# Revit family: Haworth_XSeries_Pedestal
name_source: partatom
category: Furniture Systems
units: mm (PartAtom-declared; Revit-internal decimal feet)

## family parameters
Always vertical = Yes
Cut with Voids When Loaded = No
OmniClass Number = 23.40.70.14.64.21
OmniClass Title = Systems Furniture
Part Type = Normal
Room Calculation Point = No
Round Connector Dimension = Use Diameter
Shared = No
Work Plane-Based = No

## types (10) — shared parameters
2 Drawers = Yes
Actual Depth = 23"
Actual Width = 15"
Assembly Code = E2020200
Classic Pull = No
Crescent Pull = No
Custom Size = No
Depth = 23"
Description = Haworth XSeries Pedestal
Drawer 1 Height = 11 7/8"
Drawer 4 Height = 2 7/8"
Ellipse Pull = No
J Pull = No
Linear Pull = Yes
Manufacturer = Haworth
Max. Depth = 29"
Max. Height = 27 3/4"
Min. Depth = 17"
Min. Height = 21 1/2"
Model = JPHQ-24
Pull Finish = Haworth _ Metal _ Brushed Aluminum
Radius Pull = No
Revision Number = 5
Size = Verify Final Dim. w/ Haworth
Standard Depths = 17, 23, 29 in
Sustainability Info = https://www.haworth.com
Taper Pull = No
Tug = No
URL = http://www.haworth.com
URL - Product = https://www.haworth.com
Warranty = https://cdn.shopify.com

## per-type parameters (varying)
| type | 3 Drawers | 4 Drawers | Actual Height | Box Box File | Box File | Casters | Cushion | Drawer 2 Height | Drawer 3 Height | Drawer 3 Offset | File File | Pencil Box File | Pencil Pencil Box File | Plynth Base | Standard Heights | Total Drawer Height |
| 23d 15w 27h - Pencil Pencil Box File - Mobile | Yes | Yes | 27 1/2" | No | No | Yes | Yes | 5 7/8" | 2 7/8" | 3 1/8" | No | No | Yes | No | 27.5 in. | 24 1/8" |
| 23d 15w 21h - Box File - Mobile | No | No | 21 1/2" | No | Yes | Yes | Yes | 5 7/8" | 2 7/8" | 1/8" | No | No | No | No | 21.5 in. | 18 1/8" |
| 23d 15w 24h - Pencil Box File - Mobile | Yes | No | 24 1/2" | No | No | Yes | Yes | 5 7/8" | 2 7/8" | 1/8" | No | Yes | No | No | 24.5 in. | 21 1/8" |
| 23d 15w 27h - Box Box File - Mobile | Yes | No | 27 1/2" | Yes | No | Yes | Yes | 5 7/8" | 5 7/8" | 1/8" | No | No | No | No | 27.5 in. | 24 1/8" |
| 23d 15w 27h - File File - Mobile | No | No | 27 1/2" | No | No | Yes | Yes | 11 7/8" | 2 7/8" | 1/8" | Yes | No | No | No | 27.5 in. | 24 1/8" |
| 23d 15w 27h - Box Box File - Suspended | Yes | No | 27 1/2" | Yes | No | No | No | 5 7/8" | 5 7/8" | 1/8" | No | No | No | Yes | 27.5 in. | 24 1/8" |
| 23d 15w 24h - Pencil Box File - Suspended | Yes | No | 24 1/2" | No | No | No | No | 5 7/8" | 2 7/8" | 1/8" | No | Yes | No | Yes | 24.5 in. | 21 1/8" |
| 23d 15w 21h - Box File - Suspended | No | No | 21 1/2" | No | Yes | No | No | 5 7/8" | 2 7/8" | 1/8" | No | No | No | Yes | 21.5 in. | 18 1/8" |
| 23d 15w 27h - Pencil Pencil Box File - Suspended | Yes | Yes | 27 1/2" | No | No | No | No | 5 7/8" | 2 7/8" | 3 1/8" | No | No | Yes | Yes | 27.5 in. | 24 1/8" |
| 23d 15w 27h - File File - Suspended | No | No | 27 1/2" | No | No | No | No | 11 7/8" | 2 7/8" | 1/8" | Yes | No | No | Yes | 27.5 in. | 24 1/8" |

## geometry (parser evidence)
native form markers: Sweep x16
no freeform markers — native parametric forms only
